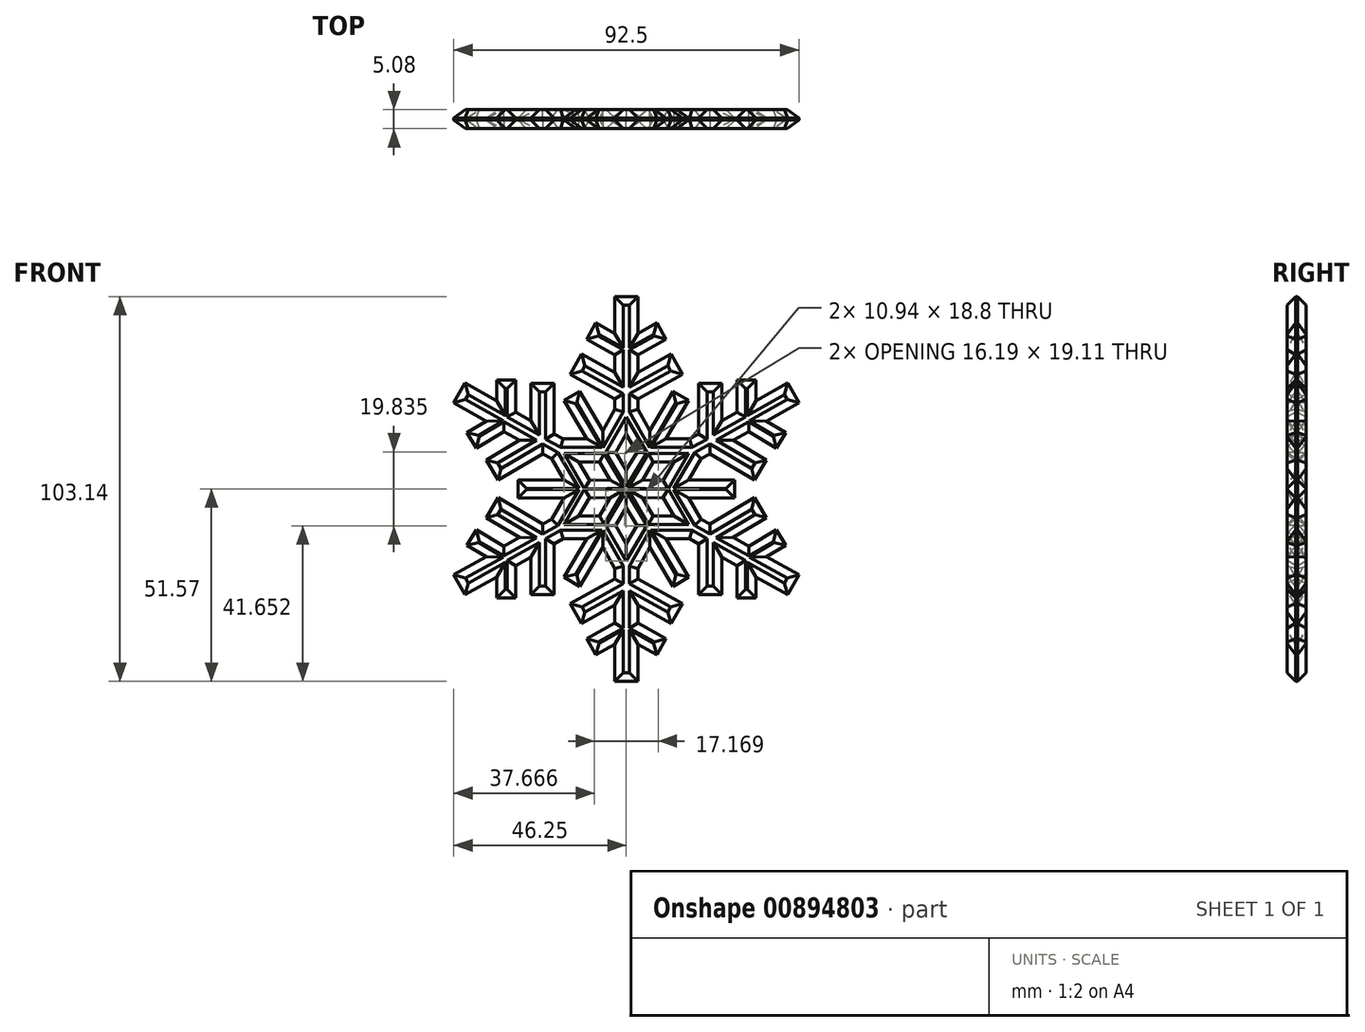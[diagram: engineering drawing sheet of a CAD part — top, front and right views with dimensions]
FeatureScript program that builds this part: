
annotation { "Feature Type Name" : "Feature", "Feature Type Description" : "" }
export const myFeature = defineFeature(function(context is Context, id is Id, definition is map)
    precondition{}
    {
        {
            var Q0;
            Q0=qCreatedBy(makeId("Front.planeOp"),FACE);
            var sketch = newSketch(context, id + "F0", { "sketchPlane" : qUnion([Q0])});
            skLineSegment(sketch, "E0", {"start": v(0, -5) * mm, "end": v(-2.83, -9.77) * mm});
            skLineSegment(sketch, "E1", {"start": v(-2.83, -9.77) * mm, "end": v(0, -14.71) * mm});
            skLineSegment(sketch, "E2", {"start": v(0, -51.57) * mm, "end": v(-3.12, -51.57) * mm});
            skLineSegment(sketch, "E3", {"start": v(-3.12, -51.57) * mm, "end": v(-3.12, -41.68) * mm});
            skLineSegment(sketch, "E4", {"start": v(-3.12, -41.68) * mm, "end": v(-8.18, -44.5) * mm});
            skLineSegment(sketch, "E5", {"start": v(-8.18, -44.5) * mm, "end": v(-10.6, -40.16) * mm});
            skLineSegment(sketch, "E6", {"start": v(-10.6, -40.16) * mm, "end": v(-3.12, -35.98) * mm});
            skLineSegment(sketch, "E7", {"start": v(-3.12, -35.98) * mm, "end": v(-3.12, -31.16) * mm});
            skLineSegment(sketch, "E8", {"start": v(-3.12, -31.16) * mm, "end": v(-12, -36.12) * mm});
            skLineSegment(sketch, "E9", {"start": v(-12, -36.12) * mm, "end": v(-15, -30.75) * mm});
            skLineSegment(sketch, "E10", {"start": v(-15, -30.75) * mm, "end": v(-3.12, -24.11) * mm});
            skLineSegment(sketch, "E11", {"start": v(-3.12, -24.11) * mm, "end": v(-3.12, -21.32) * mm});
            skLineSegment(sketch, "E12", {"start": v(-3.12, -21.32) * mm, "end": v(-6.29, -15.65) * mm});
            skLineSegment(sketch, "E13", {"start": v(-6.29, -15.65) * mm, "end": v(-12.51, -26.16) * mm});
            skLineSegment(sketch, "E14", {"start": v(-12.51, -26.16) * mm, "end": v(-16.68, -23.7) * mm});
            skLineSegment(sketch, "E15", {"start": v(-16.68, -23.7) * mm, "end": v(-10.57, -13.4) * mm});
            skLineSegment(sketch, "E16", {"start": v(-10.57, -13.4) * mm, "end": v(-17, -13.4) * mm});
            skLineSegment(sketch, "E17", {"start": v(-17, -13.4) * mm, "end": v(-19.37, -14.71) * mm});
            skLineSegment(sketch, "E18", {"start": v(-19.37, -14.71) * mm, "end": v(-19.37, -28.34) * mm});
            skLineSegment(sketch, "E19", {"start": v(-19.37, -28.34) * mm, "end": v(-25.64, -28.34) * mm});
            skLineSegment(sketch, "E20", {"start": v(-25.64, -28.34) * mm, "end": v(-25.64, -18.32) * mm});
            skLineSegment(sketch, "E21", {"start": v(-25.64, -18.32) * mm, "end": v(-29.69, -20.58) * mm});
            skLineSegment(sketch, "E22", {"start": v(-29.69, -20.58) * mm, "end": v(-29.69, -29.2) * mm});
            skLineSegment(sketch, "E23", {"start": v(-29.69, -29.2) * mm, "end": v(-34.73, -29.2) * mm});
            skLineSegment(sketch, "E24", {"start": v(-34.73, -29.2) * mm, "end": v(-34.73, -23.6) * mm});
            skLineSegment(sketch, "E25", {"start": v(-34.73, -23.6) * mm, "end": v(-43.27, -28.37) * mm});
            skLineSegment(sketch, "E26", {"start": v(-43.27, -28.37) * mm, "end": v(-46.25, -23.04) * mm});
            skLineSegment(sketch, "E27", {"start": v(-46.25, -23.04) * mm, "end": v(-37.55, -18.19) * mm});
            skLineSegment(sketch, "E28", {"start": v(-37.55, -18.19) * mm, "end": v(-42.7, -15.14) * mm});
            skLineSegment(sketch, "E29", {"start": v(-42.7, -15.14) * mm, "end": v(-40.22, -10.95) * mm});
            skLineSegment(sketch, "E30", {"start": v(-40.22, -10.95) * mm, "end": v(-32.83, -15.33) * mm});
            skLineSegment(sketch, "E31", {"start": v(-32.83, -15.33) * mm, "end": v(-28.66, -13) * mm});
            skLineSegment(sketch, "E32", {"start": v(-28.66, -13) * mm, "end": v(-37.57, -7.73) * mm});
            skLineSegment(sketch, "E33", {"start": v(-37.57, -7.73) * mm, "end": v(-34.38, -2.34) * mm});
            skLineSegment(sketch, "E34", {"start": v(-34.38, -2.34) * mm, "end": v(-22.4, -9.44) * mm});
            skLineSegment(sketch, "E35", {"start": v(-22.4, -9.44) * mm, "end": v(-20.03, -8.12) * mm});
            skLineSegment(sketch, "E36", {"start": v(-20.03, -8.12) * mm, "end": v(-16.64, -2.4) * mm});
            skLineSegment(sketch, "E37", {"start": v(-16.64, -2.4) * mm, "end": v(-29.06, -2.4) * mm});
            skLineSegment(sketch, "E38", {"start": v(-29.06, -2.4) * mm, "end": v(-29.06, 0) * mm});
            skLineSegment(sketch, "E39", {"start": v(0, 0) * mm, "end": v(0, -1.87) * mm});
            skLineSegment(sketch, "E40", {"start": v(0, 0) * mm, "end": v(2.1, 0) * mm});
            skLineSegment(sketch, "E41", {"start": v(0, 0) * mm, "end": v(-2.42, 0) * mm});
            skLineSegment(sketch, "E42", {"start": v(0, 0) * mm, "end": v(0, 1.78) * mm});
            skLineSegment(sketch, "E43.MirrorCS", {"start": v(0, -5) * mm, "end": v(2.83, -9.77) * mm});
            skLineSegment(sketch, "E44.MirrorCS", {"start": v(2.83, -9.77) * mm, "end": v(0, -14.71) * mm});
            skLineSegment(sketch, "E45", {"start": v(-4.39, -2.4) * mm, "end": v(-7.18, -7.27) * mm});
            skLineSegment(sketch, "E46", {"start": v(-7.18, -7.27) * mm, "end": v(-12.74, -7.27) * mm});
            skLineSegment(sketch, "E47", {"start": v(-12.74, -7.27) * mm, "end": v(-9.89, -2.29) * mm});
            skLineSegment(sketch, "E48", {"start": v(-9.89, -2.29) * mm, "end": v(-4.39, -2.4) * mm});
            skLineSegment(sketch, "E49.MirrorCS", {"start": v(4.39, -2.4) * mm, "end": v(7.18, -7.27) * mm});
            skLineSegment(sketch, "E50.MirrorCS", {"start": v(9.89, -2.29) * mm, "end": v(4.39, -2.4) * mm});
            skLineSegment(sketch, "E51.MirrorCS", {"start": v(7.18, -7.27) * mm, "end": v(12.74, -7.27) * mm});
            skLineSegment(sketch, "E52.MirrorCS", {"start": v(12.74, -7.27) * mm, "end": v(9.89, -2.29) * mm});
            skLineSegment(sketch, "E53.MirrorCS", {"start": v(0, -51.57) * mm, "end": v(3.12, -51.57) * mm});
            skLineSegment(sketch, "E54.MirrorCS", {"start": v(3.12, -51.57) * mm, "end": v(3.12, -41.68) * mm});
            skLineSegment(sketch, "E55.MirrorCS", {"start": v(3.12, -41.68) * mm, "end": v(8.18, -44.5) * mm});
            skLineSegment(sketch, "E56.MirrorCS", {"start": v(8.18, -44.5) * mm, "end": v(10.6, -40.16) * mm});
            skLineSegment(sketch, "E57.MirrorCS", {"start": v(10.6, -40.16) * mm, "end": v(3.12, -35.98) * mm});
            skLineSegment(sketch, "E58.MirrorCS", {"start": v(3.12, -35.98) * mm, "end": v(3.12, -31.16) * mm});
            skLineSegment(sketch, "E59.MirrorCS", {"start": v(3.12, -31.16) * mm, "end": v(12, -36.12) * mm});
            skLineSegment(sketch, "E60.MirrorCS", {"start": v(12, -36.12) * mm, "end": v(15, -30.75) * mm});
            skLineSegment(sketch, "E61.MirrorCS", {"start": v(15, -30.75) * mm, "end": v(3.12, -24.11) * mm});
            skLineSegment(sketch, "E62.MirrorCS", {"start": v(3.12, -24.11) * mm, "end": v(3.12, -21.32) * mm});
            skLineSegment(sketch, "E63.MirrorCS", {"start": v(3.12, -21.32) * mm, "end": v(6.29, -15.65) * mm});
            skLineSegment(sketch, "E64.MirrorCS", {"start": v(6.29, -15.65) * mm, "end": v(12.51, -26.16) * mm});
            skLineSegment(sketch, "E65.MirrorCS", {"start": v(12.51, -26.16) * mm, "end": v(16.68, -23.7) * mm});
            skLineSegment(sketch, "E66.MirrorCS", {"start": v(16.68, -23.7) * mm, "end": v(10.57, -13.4) * mm});
            skLineSegment(sketch, "E67.MirrorCS", {"start": v(10.57, -13.4) * mm, "end": v(17, -13.4) * mm});
            skLineSegment(sketch, "E68.MirrorCS", {"start": v(17, -13.4) * mm, "end": v(19.37, -14.71) * mm});
            skLineSegment(sketch, "E69.MirrorCS", {"start": v(19.37, -14.71) * mm, "end": v(19.37, -28.34) * mm});
            skLineSegment(sketch, "E70.MirrorCS", {"start": v(19.37, -28.34) * mm, "end": v(25.64, -28.34) * mm});
            skLineSegment(sketch, "E71.MirrorCS", {"start": v(25.64, -28.34) * mm, "end": v(25.64, -18.32) * mm});
            skLineSegment(sketch, "E72.MirrorCS", {"start": v(25.64, -18.32) * mm, "end": v(29.69, -20.58) * mm});
            skLineSegment(sketch, "E73.MirrorCS", {"start": v(29.69, -20.58) * mm, "end": v(29.69, -29.2) * mm});
            skLineSegment(sketch, "E74.MirrorCS", {"start": v(29.69, -29.2) * mm, "end": v(34.73, -29.2) * mm});
            skLineSegment(sketch, "E75.MirrorCS", {"start": v(34.73, -29.2) * mm, "end": v(34.73, -23.6) * mm});
            skLineSegment(sketch, "E76.MirrorCS", {"start": v(34.73, -23.6) * mm, "end": v(43.27, -28.37) * mm});
            skLineSegment(sketch, "E77.MirrorCS", {"start": v(43.27, -28.37) * mm, "end": v(46.25, -23.04) * mm});
            skLineSegment(sketch, "E78.MirrorCS", {"start": v(46.25, -23.04) * mm, "end": v(37.55, -18.19) * mm});
            skLineSegment(sketch, "E79.MirrorCS", {"start": v(37.55, -18.19) * mm, "end": v(42.7, -15.14) * mm});
            skLineSegment(sketch, "E80.MirrorCS", {"start": v(42.7, -15.14) * mm, "end": v(40.22, -10.95) * mm});
            skLineSegment(sketch, "E81.MirrorCS", {"start": v(40.22, -10.95) * mm, "end": v(32.83, -15.33) * mm});
            skLineSegment(sketch, "E82.MirrorCS", {"start": v(32.83, -15.33) * mm, "end": v(28.66, -13) * mm});
            skLineSegment(sketch, "E83.MirrorCS", {"start": v(28.66, -13) * mm, "end": v(37.57, -7.73) * mm});
            skLineSegment(sketch, "E84.MirrorCS", {"start": v(37.57, -7.73) * mm, "end": v(34.38, -2.34) * mm});
            skLineSegment(sketch, "E85.MirrorCS", {"start": v(34.38, -2.34) * mm, "end": v(22.4, -9.44) * mm});
            skLineSegment(sketch, "E86.MirrorCS", {"start": v(22.4, -9.44) * mm, "end": v(20.03, -8.12) * mm});
            skLineSegment(sketch, "E87.MirrorCS", {"start": v(20.03, -8.12) * mm, "end": v(16.64, -2.4) * mm});
            skLineSegment(sketch, "E88.MirrorCS", {"start": v(16.64, -2.4) * mm, "end": v(29.06, -2.4) * mm});
            skLineSegment(sketch, "E89.MirrorCS", {"start": v(29.06, -2.4) * mm, "end": v(29.06, 0) * mm});
            skLineSegment(sketch, "E90.MirrorCS", {"start": v(9.89, 2.29) * mm, "end": v(4.39, 2.4) * mm});
            skLineSegment(sketch, "E91.MirrorCS", {"start": v(4.39, 2.4) * mm, "end": v(7.18, 7.27) * mm});
            skLineSegment(sketch, "E92.MirrorCS", {"start": v(12.74, 7.27) * mm, "end": v(9.89, 2.29) * mm});
            skLineSegment(sketch, "E93.MirrorCS", {"start": v(7.18, 7.27) * mm, "end": v(12.74, 7.27) * mm});
            skLineSegment(sketch, "E94.MirrorCS", {"start": v(29.06, 2.4) * mm, "end": v(29.06, 0) * mm});
            skLineSegment(sketch, "E95.MirrorCS", {"start": v(16.64, 2.4) * mm, "end": v(29.06, 2.4) * mm});
            skLineSegment(sketch, "E96.MirrorCS", {"start": v(20.03, 8.12) * mm, "end": v(16.64, 2.4) * mm});
            skLineSegment(sketch, "E97.MirrorCS", {"start": v(22.4, 9.44) * mm, "end": v(20.03, 8.12) * mm});
            skLineSegment(sketch, "E98.MirrorCS", {"start": v(34.38, 2.34) * mm, "end": v(22.4, 9.44) * mm});
            skLineSegment(sketch, "E99.MirrorCS", {"start": v(37.57, 7.73) * mm, "end": v(34.38, 2.34) * mm});
            skLineSegment(sketch, "E100.MirrorCS", {"start": v(28.66, 13) * mm, "end": v(37.57, 7.73) * mm});
            skLineSegment(sketch, "E101.MirrorCS", {"start": v(32.83, 15.33) * mm, "end": v(28.66, 13) * mm});
            skLineSegment(sketch, "E102.MirrorCS", {"start": v(40.22, 10.95) * mm, "end": v(32.83, 15.33) * mm});
            skLineSegment(sketch, "E103.MirrorCS", {"start": v(42.7, 15.14) * mm, "end": v(40.22, 10.95) * mm});
            skLineSegment(sketch, "E104.MirrorCS", {"start": v(37.55, 18.19) * mm, "end": v(42.7, 15.14) * mm});
            skLineSegment(sketch, "E105.MirrorCS", {"start": v(46.25, 23.04) * mm, "end": v(37.55, 18.19) * mm});
            skLineSegment(sketch, "E106.MirrorCS", {"start": v(29.69, 20.58) * mm, "end": v(29.69, 29.2) * mm});
            skLineSegment(sketch, "E107.MirrorCS", {"start": v(43.27, 28.37) * mm, "end": v(46.25, 23.04) * mm});
            skLineSegment(sketch, "E108.MirrorCS", {"start": v(25.64, 28.34) * mm, "end": v(25.64, 18.32) * mm});
            skLineSegment(sketch, "E109.MirrorCS", {"start": v(34.73, 29.2) * mm, "end": v(34.73, 23.6) * mm});
            skLineSegment(sketch, "E110.MirrorCS", {"start": v(19.37, 28.34) * mm, "end": v(25.64, 28.34) * mm});
            skLineSegment(sketch, "E111.MirrorCS", {"start": v(29.69, 29.2) * mm, "end": v(34.73, 29.2) * mm});
            skLineSegment(sketch, "E112.MirrorCS", {"start": v(34.73, 23.6) * mm, "end": v(43.27, 28.37) * mm});
            skLineSegment(sketch, "E113.MirrorCS", {"start": v(19.37, 14.71) * mm, "end": v(19.37, 28.34) * mm});
            skLineSegment(sketch, "E114.MirrorCS", {"start": v(-3.12, 24.11) * mm, "end": v(-3.12, 21.32) * mm});
            skLineSegment(sketch, "E115.MirrorCS", {"start": v(-25.64, 18.32) * mm, "end": v(-29.69, 20.58) * mm});
            skLineSegment(sketch, "E116.MirrorCS", {"start": v(-17, 13.4) * mm, "end": v(-19.37, 14.71) * mm});
            skLineSegment(sketch, "E117.MirrorCS", {"start": v(12.51, 26.16) * mm, "end": v(16.68, 23.7) * mm});
            skLineSegment(sketch, "E118.MirrorCS", {"start": v(3.12, 24.11) * mm, "end": v(3.12, 21.32) * mm});
            skLineSegment(sketch, "E119.MirrorCS", {"start": v(12, 36.12) * mm, "end": v(15, 30.75) * mm});
            skLineSegment(sketch, "E120.MirrorCS", {"start": v(3.12, 21.32) * mm, "end": v(6.29, 15.65) * mm});
            skLineSegment(sketch, "E121.MirrorCS", {"start": v(-10.57, 13.4) * mm, "end": v(-17, 13.4) * mm});
            skLineSegment(sketch, "E122.MirrorCS", {"start": v(-28.66, 13) * mm, "end": v(-37.57, 7.73) * mm});
            skLineSegment(sketch, "E123.MirrorCS", {"start": v(-6.29, 15.65) * mm, "end": v(-12.51, 26.16) * mm});
            skLineSegment(sketch, "E124.MirrorCS", {"start": v(3.12, 41.68) * mm, "end": v(8.18, 44.5) * mm});
            skLineSegment(sketch, "E125.MirrorCS", {"start": v(-34.73, 23.6) * mm, "end": v(-43.27, 28.37) * mm});
            skLineSegment(sketch, "E126.MirrorCS", {"start": v(-3.12, 41.68) * mm, "end": v(-8.18, 44.5) * mm});
            skLineSegment(sketch, "E127.MirrorCS", {"start": v(-2.83, 9.77) * mm, "end": v(0, 14.71) * mm});
            skLineSegment(sketch, "E128.MirrorCS", {"start": v(-10.6, 40.16) * mm, "end": v(-3.12, 35.98) * mm});
            skLineSegment(sketch, "E129.MirrorCS", {"start": v(2.83, 9.77) * mm, "end": v(0, 14.71) * mm});
            skLineSegment(sketch, "E130.MirrorCS", {"start": v(10.57, 13.4) * mm, "end": v(17, 13.4) * mm});
            skLineSegment(sketch, "E131.MirrorCS", {"start": v(-3.12, 31.16) * mm, "end": v(-12, 36.12) * mm});
            skLineSegment(sketch, "E132.MirrorCS", {"start": v(-3.12, 51.57) * mm, "end": v(-3.12, 41.68) * mm});
            skLineSegment(sketch, "E133.MirrorCS", {"start": v(-3.12, 35.98) * mm, "end": v(-3.12, 31.16) * mm});
            skLineSegment(sketch, "E134.MirrorCS", {"start": v(-29.69, 20.58) * mm, "end": v(-29.69, 29.2) * mm});
            skLineSegment(sketch, "E135.MirrorCS", {"start": v(-3.12, 21.32) * mm, "end": v(-6.29, 15.65) * mm});
            skLineSegment(sketch, "E136.MirrorCS", {"start": v(-43.27, 28.37) * mm, "end": v(-46.25, 23.04) * mm});
            skLineSegment(sketch, "E137.MirrorCS", {"start": v(-40.22, 10.95) * mm, "end": v(-32.83, 15.33) * mm});
            skLineSegment(sketch, "E138.MirrorCS", {"start": v(-19.37, 14.71) * mm, "end": v(-19.37, 28.34) * mm});
            skLineSegment(sketch, "E139.MirrorCS", {"start": v(-12, 36.12) * mm, "end": v(-15, 30.75) * mm});
            skLineSegment(sketch, "E140.MirrorCS", {"start": v(-42.7, 15.14) * mm, "end": v(-40.22, 10.95) * mm});
            skLineSegment(sketch, "E141.MirrorCS", {"start": v(-25.64, 28.34) * mm, "end": v(-25.64, 18.32) * mm});
            skLineSegment(sketch, "E142.MirrorCS", {"start": v(8.18, 44.5) * mm, "end": v(10.6, 40.16) * mm});
            skLineSegment(sketch, "E143.MirrorCS", {"start": v(-46.25, 23.04) * mm, "end": v(-37.55, 18.19) * mm});
            skLineSegment(sketch, "E144.MirrorCS", {"start": v(-32.83, 15.33) * mm, "end": v(-28.66, 13) * mm});
            skLineSegment(sketch, "E145.MirrorCS", {"start": v(3.12, 51.57) * mm, "end": v(3.12, 41.68) * mm});
            skLineSegment(sketch, "E146.MirrorCS", {"start": v(-12.51, 26.16) * mm, "end": v(-16.68, 23.7) * mm});
            skLineSegment(sketch, "E147.MirrorCS", {"start": v(-8.18, 44.5) * mm, "end": v(-10.6, 40.16) * mm});
            skLineSegment(sketch, "E148.MirrorCS", {"start": v(10.6, 40.16) * mm, "end": v(3.12, 35.98) * mm});
            skLineSegment(sketch, "E149.MirrorCS", {"start": v(3.12, 35.98) * mm, "end": v(3.12, 31.16) * mm});
            skLineSegment(sketch, "E150.MirrorCS", {"start": v(-16.68, 23.7) * mm, "end": v(-10.57, 13.4) * mm});
            skLineSegment(sketch, "E151.MirrorCS", {"start": v(-29.69, 29.2) * mm, "end": v(-34.73, 29.2) * mm});
            skLineSegment(sketch, "E152.MirrorCS", {"start": v(15, 30.75) * mm, "end": v(3.12, 24.11) * mm});
            skLineSegment(sketch, "E153.MirrorCS", {"start": v(-34.73, 29.2) * mm, "end": v(-34.73, 23.6) * mm});
            skLineSegment(sketch, "E154.MirrorCS", {"start": v(16.68, 23.7) * mm, "end": v(10.57, 13.4) * mm});
            skLineSegment(sketch, "E155.MirrorCS", {"start": v(-15, 30.75) * mm, "end": v(-3.12, 24.11) * mm});
            skLineSegment(sketch, "E156.MirrorCS", {"start": v(6.29, 15.65) * mm, "end": v(12.51, 26.16) * mm});
            skLineSegment(sketch, "E157.MirrorCS", {"start": v(-37.55, 18.19) * mm, "end": v(-42.7, 15.14) * mm});
            skLineSegment(sketch, "E158.MirrorCS", {"start": v(3.12, 31.16) * mm, "end": v(12, 36.12) * mm});
            skLineSegment(sketch, "E159.MirrorCS", {"start": v(-19.37, 28.34) * mm, "end": v(-25.64, 28.34) * mm});
            skLineSegment(sketch, "E160.MirrorCS", {"start": v(0, 51.57) * mm, "end": v(-3.12, 51.57) * mm});
            skLineSegment(sketch, "E161.MirrorCS", {"start": v(0, 51.57) * mm, "end": v(3.12, 51.57) * mm});
            skLineSegment(sketch, "E162.MirrorCS", {"start": v(0, 0) * mm, "end": v(0, 1.87) * mm});
            skLineSegment(sketch, "E163.MirrorCS", {"start": v(-22.4, 9.44) * mm, "end": v(-20.03, 8.12) * mm});
            skLineSegment(sketch, "E164.MirrorCS", {"start": v(0, 5) * mm, "end": v(2.83, 9.77) * mm});
            skLineSegment(sketch, "E165.MirrorCS", {"start": v(-29.06, 2.4) * mm, "end": v(-29.06, 0) * mm});
            skLineSegment(sketch, "E166.MirrorCS", {"start": v(0, 5) * mm, "end": v(-2.83, 9.77) * mm});
            skLineSegment(sketch, "E167.MirrorCS", {"start": v(-9.89, 2.29) * mm, "end": v(-4.39, 2.4) * mm});
            skLineSegment(sketch, "E168.MirrorCS", {"start": v(-7.18, 7.27) * mm, "end": v(-12.74, 7.27) * mm});
            skLineSegment(sketch, "E169.MirrorCS", {"start": v(-20.03, 8.12) * mm, "end": v(-16.64, 2.4) * mm});
            skLineSegment(sketch, "E170.MirrorCS", {"start": v(-37.57, 7.73) * mm, "end": v(-34.38, 2.34) * mm});
            skLineSegment(sketch, "E171.MirrorCS", {"start": v(-12.74, 7.27) * mm, "end": v(-9.89, 2.29) * mm});
            skLineSegment(sketch, "E172.MirrorCS", {"start": v(-16.64, 2.4) * mm, "end": v(-29.06, 2.4) * mm});
            skLineSegment(sketch, "E173.MirrorCS", {"start": v(-4.39, 2.4) * mm, "end": v(-7.18, 7.27) * mm});
            skLineSegment(sketch, "E174.MirrorCS", {"start": v(-34.38, 2.34) * mm, "end": v(-22.4, 9.44) * mm});
            skLineSegment(sketch, "E175", {"start": v(17, 13.4) * mm, "end": v(19.37, 14.71) * mm});
            skLineSegment(sketch, "E176", {"start": v(25.64, 18.32) * mm, "end": v(29.69, 20.58) * mm});
            skSolve(sketch);
        }
        {
            var Q0;
            Q0=makeQuery(id+"F0.imprint","IMPRINT",FACE,{"disambiguationData":[TD([[makeQuery(id+"F0.imprint","IMPRINT",EDGE,{"derivedFrom":sQuery(id+"F0.wireOp",EDGE,"E0")}),-1.0]])]});
            extrude(context, id + "F1", {"entities" : qUnion([Q0]), "depth" : 2.54 * mm, "offsetDistance" : 25.4 * mm});
        }
        {
            var Q0;
            Q0=makeQuery(id+"F1.opExtrude","CAP_FACE",FACE,{"disambiguationData":[OSD([sQuery(id+"F0.wireOp",EDGE,"E0"),sQuery(id+"F0.wireOp",EDGE,"E1"),sQuery(id+"F0.wireOp",EDGE,"E2"),sQuery(id+"F0.wireOp",EDGE,"E3"),sQuery(id+"F0.wireOp",EDGE,"E4"),sQuery(id+"F0.wireOp",EDGE,"E5"),sQuery(id+"F0.wireOp",EDGE,"E6"),sQuery(id+"F0.wireOp",EDGE,"E7"),sQuery(id+"F0.wireOp",EDGE,"E8"),sQuery(id+"F0.wireOp",EDGE,"E9"),sQuery(id+"F0.wireOp",EDGE,"E10"),sQuery(id+"F0.wireOp",EDGE,"E11"),sQuery(id+"F0.wireOp",EDGE,"E12"),sQuery(id+"F0.wireOp",EDGE,"E13"),sQuery(id+"F0.wireOp",EDGE,"E14"),sQuery(id+"F0.wireOp",EDGE,"E15"),sQuery(id+"F0.wireOp",EDGE,"E16"),sQuery(id+"F0.wireOp",EDGE,"E17"),sQuery(id+"F0.wireOp",EDGE,"E18"),sQuery(id+"F0.wireOp",EDGE,"E19"),sQuery(id+"F0.wireOp",EDGE,"E20"),sQuery(id+"F0.wireOp",EDGE,"E21"),sQuery(id+"F0.wireOp",EDGE,"E22"),sQuery(id+"F0.wireOp",EDGE,"E23"),sQuery(id+"F0.wireOp",EDGE,"E24"),sQuery(id+"F0.wireOp",EDGE,"E25"),sQuery(id+"F0.wireOp",EDGE,"E26"),sQuery(id+"F0.wireOp",EDGE,"E27"),sQuery(id+"F0.wireOp",EDGE,"E28"),sQuery(id+"F0.wireOp",EDGE,"E29"),sQuery(id+"F0.wireOp",EDGE,"E30"),sQuery(id+"F0.wireOp",EDGE,"E31"),sQuery(id+"F0.wireOp",EDGE,"E32"),sQuery(id+"F0.wireOp",EDGE,"E33"),sQuery(id+"F0.wireOp",EDGE,"E34"),sQuery(id+"F0.wireOp",EDGE,"E35"),sQuery(id+"F0.wireOp",EDGE,"E36"),sQuery(id+"F0.wireOp",EDGE,"E37"),sQuery(id+"F0.wireOp",EDGE,"E38"),sQuery(id+"F0.wireOp",EDGE,"E43.MirrorCS"),sQuery(id+"F0.wireOp",EDGE,"E44.MirrorCS"),sQuery(id+"F0.wireOp",EDGE,"E45"),sQuery(id+"F0.wireOp",EDGE,"E46"),sQuery(id+"F0.wireOp",EDGE,"E47"),sQuery(id+"F0.wireOp",EDGE,"E48"),sQuery(id+"F0.wireOp",EDGE,"E49.MirrorCS"),sQuery(id+"F0.wireOp",EDGE,"E50.MirrorCS"),sQuery(id+"F0.wireOp",EDGE,"E51.MirrorCS"),sQuery(id+"F0.wireOp",EDGE,"E52.MirrorCS"),sQuery(id+"F0.wireOp",EDGE,"E53.MirrorCS"),sQuery(id+"F0.wireOp",EDGE,"E54.MirrorCS"),sQuery(id+"F0.wireOp",EDGE,"E55.MirrorCS"),sQuery(id+"F0.wireOp",EDGE,"E56.MirrorCS"),sQuery(id+"F0.wireOp",EDGE,"E57.MirrorCS"),sQuery(id+"F0.wireOp",EDGE,"E58.MirrorCS"),sQuery(id+"F0.wireOp",EDGE,"E59.MirrorCS"),sQuery(id+"F0.wireOp",EDGE,"E60.MirrorCS"),sQuery(id+"F0.wireOp",EDGE,"E61.MirrorCS"),sQuery(id+"F0.wireOp",EDGE,"E62.MirrorCS"),sQuery(id+"F0.wireOp",EDGE,"E63.MirrorCS"),sQuery(id+"F0.wireOp",EDGE,"E64.MirrorCS"),sQuery(id+"F0.wireOp",EDGE,"E65.MirrorCS"),sQuery(id+"F0.wireOp",EDGE,"E66.MirrorCS"),sQuery(id+"F0.wireOp",EDGE,"E67.MirrorCS"),sQuery(id+"F0.wireOp",EDGE,"E68.MirrorCS"),sQuery(id+"F0.wireOp",EDGE,"E69.MirrorCS"),sQuery(id+"F0.wireOp",EDGE,"E70.MirrorCS"),sQuery(id+"F0.wireOp",EDGE,"E71.MirrorCS"),sQuery(id+"F0.wireOp",EDGE,"E72.MirrorCS"),sQuery(id+"F0.wireOp",EDGE,"E73.MirrorCS"),sQuery(id+"F0.wireOp",EDGE,"E74.MirrorCS"),sQuery(id+"F0.wireOp",EDGE,"E75.MirrorCS"),sQuery(id+"F0.wireOp",EDGE,"E76.MirrorCS"),sQuery(id+"F0.wireOp",EDGE,"E77.MirrorCS"),sQuery(id+"F0.wireOp",EDGE,"E78.MirrorCS"),sQuery(id+"F0.wireOp",EDGE,"E79.MirrorCS"),sQuery(id+"F0.wireOp",EDGE,"E80.MirrorCS"),sQuery(id+"F0.wireOp",EDGE,"E81.MirrorCS"),sQuery(id+"F0.wireOp",EDGE,"E82.MirrorCS"),sQuery(id+"F0.wireOp",EDGE,"E83.MirrorCS"),sQuery(id+"F0.wireOp",EDGE,"E84.MirrorCS"),sQuery(id+"F0.wireOp",EDGE,"E85.MirrorCS"),sQuery(id+"F0.wireOp",EDGE,"E86.MirrorCS"),sQuery(id+"F0.wireOp",EDGE,"E87.MirrorCS"),sQuery(id+"F0.wireOp",EDGE,"E88.MirrorCS"),sQuery(id+"F0.wireOp",EDGE,"E89.MirrorCS"),sQuery(id+"F0.wireOp",EDGE,"E94.MirrorCS"),sQuery(id+"F0.wireOp",EDGE,"E95.MirrorCS"),sQuery(id+"F0.wireOp",EDGE,"E96.MirrorCS"),sQuery(id+"F0.wireOp",EDGE,"E97.MirrorCS"),sQuery(id+"F0.wireOp",EDGE,"E98.MirrorCS"),sQuery(id+"F0.wireOp",EDGE,"E99.MirrorCS"),sQuery(id+"F0.wireOp",EDGE,"E100.MirrorCS"),sQuery(id+"F0.wireOp",EDGE,"E101.MirrorCS"),sQuery(id+"F0.wireOp",EDGE,"E102.MirrorCS"),sQuery(id+"F0.wireOp",EDGE,"E103.MirrorCS"),sQuery(id+"F0.wireOp",EDGE,"E104.MirrorCS"),sQuery(id+"F0.wireOp",EDGE,"E105.MirrorCS"),sQuery(id+"F0.wireOp",EDGE,"E106.MirrorCS"),sQuery(id+"F0.wireOp",EDGE,"E107.MirrorCS"),sQuery(id+"F0.wireOp",EDGE,"E108.MirrorCS"),sQuery(id+"F0.wireOp",EDGE,"E109.MirrorCS"),sQuery(id+"F0.wireOp",EDGE,"E110.MirrorCS"),sQuery(id+"F0.wireOp",EDGE,"E111.MirrorCS"),sQuery(id+"F0.wireOp",EDGE,"E112.MirrorCS"),sQuery(id+"F0.wireOp",EDGE,"E113.MirrorCS"),sQuery(id+"F0.wireOp",EDGE,"E149.MirrorCS"),sQuery(id+"F0.wireOp",EDGE,"E140.MirrorCS"),sQuery(id+"F0.wireOp",EDGE,"E161.MirrorCS"),sQuery(id+"F0.wireOp",EDGE,"E144.MirrorCS"),sQuery(id+"F0.wireOp",EDGE,"E163.MirrorCS"),sQuery(id+"F0.wireOp",EDGE,"E115.MirrorCS"),sQuery(id+"F0.wireOp",EDGE,"E160.MirrorCS"),sQuery(id+"F0.wireOp",EDGE,"E164.MirrorCS"),sQuery(id+"F0.wireOp",EDGE,"E117.MirrorCS"),sQuery(id+"F0.wireOp",EDGE,"E118.MirrorCS"),sQuery(id+"F0.wireOp",EDGE,"E165.MirrorCS"),sQuery(id+"F0.wireOp",EDGE,"E146.MirrorCS"),sQuery(id+"F0.wireOp",EDGE,"E114.MirrorCS"),sQuery(id+"F0.wireOp",EDGE,"E133.MirrorCS"),sQuery(id+"F0.wireOp",EDGE,"E166.MirrorCS"),sQuery(id+"F0.wireOp",EDGE,"E116.MirrorCS"),sQuery(id+"F0.wireOp",EDGE,"E167.MirrorCS"),sQuery(id+"F0.wireOp",EDGE,"E120.MirrorCS"),sQuery(id+"F0.wireOp",EDGE,"E137.MirrorCS"),sQuery(id+"F0.wireOp",EDGE,"E119.MirrorCS"),sQuery(id+"F0.wireOp",EDGE,"E168.MirrorCS"),sQuery(id+"F0.wireOp",EDGE,"E142.MirrorCS"),sQuery(id+"F0.wireOp",EDGE,"E169.MirrorCS"),sQuery(id+"F0.wireOp",EDGE,"E151.MirrorCS"),sQuery(id+"F0.wireOp",EDGE,"E127.MirrorCS"),sQuery(id+"F0.wireOp",EDGE,"E136.MirrorCS"),sQuery(id+"F0.wireOp",EDGE,"E121.MirrorCS"),sQuery(id+"F0.wireOp",EDGE,"E126.MirrorCS"),sQuery(id+"F0.wireOp",EDGE,"E170.MirrorCS"),sQuery(id+"F0.wireOp",EDGE,"E90.MirrorCS"),sQuery(id+"F0.wireOp",EDGE,"E145.MirrorCS"),sQuery(id+"F0.wireOp",EDGE,"E128.MirrorCS"),sQuery(id+"F0.wireOp",EDGE,"E153.MirrorCS"),sQuery(id+"F0.wireOp",EDGE,"E152.MirrorCS"),sQuery(id+"F0.wireOp",EDGE,"E148.MirrorCS"),sQuery(id+"F0.wireOp",EDGE,"E155.MirrorCS"),sQuery(id+"F0.wireOp",EDGE,"E171.MirrorCS"),sQuery(id+"F0.wireOp",EDGE,"E172.MirrorCS"),sQuery(id+"F0.wireOp",EDGE,"E154.MirrorCS"),sQuery(id+"F0.wireOp",EDGE,"E173.MirrorCS"),sQuery(id+"F0.wireOp",EDGE,"E159.MirrorCS"),sQuery(id+"F0.wireOp",EDGE,"E123.MirrorCS"),sQuery(id+"F0.wireOp",EDGE,"E157.MirrorCS"),sQuery(id+"F0.wireOp",EDGE,"E132.MirrorCS"),sQuery(id+"F0.wireOp",EDGE,"E147.MirrorCS"),sQuery(id+"F0.wireOp",EDGE,"E174.MirrorCS"),sQuery(id+"F0.wireOp",EDGE,"E156.MirrorCS"),sQuery(id+"F0.wireOp",EDGE,"E141.MirrorCS"),sQuery(id+"F0.wireOp",EDGE,"E92.MirrorCS"),sQuery(id+"F0.wireOp",EDGE,"E131.MirrorCS"),sQuery(id+"F0.wireOp",EDGE,"E122.MirrorCS"),sQuery(id+"F0.wireOp",EDGE,"E135.MirrorCS"),sQuery(id+"F0.wireOp",EDGE,"E125.MirrorCS"),sQuery(id+"F0.wireOp",EDGE,"E91.MirrorCS"),sQuery(id+"F0.wireOp",EDGE,"E150.MirrorCS"),sQuery(id+"F0.wireOp",EDGE,"E124.MirrorCS"),sQuery(id+"F0.wireOp",EDGE,"E158.MirrorCS"),sQuery(id+"F0.wireOp",EDGE,"E134.MirrorCS"),sQuery(id+"F0.wireOp",EDGE,"E93.MirrorCS"),sQuery(id+"F0.wireOp",EDGE,"E139.MirrorCS"),sQuery(id+"F0.wireOp",EDGE,"E138.MirrorCS"),sQuery(id+"F0.wireOp",EDGE,"E143.MirrorCS"),sQuery(id+"F0.wireOp",EDGE,"E130.MirrorCS"),sQuery(id+"F0.wireOp",EDGE,"E129.MirrorCS"),sQuery(id+"F0.wireOp",EDGE,"E175"),sQuery(id+"F0.wireOp",EDGE,"E176")])],"isStart":true});
            extrude(context, id + "F2", {"entities" : qUnion([Q0]), "operationType" : NewBodyOperationType.ADD, "depth" : 2.54 * mm, "offsetDistance" : 25.4 * mm});
        }
        {
            var Q0;
            Q0=makeQuery(id+"F1.opExtrude","CAP_FACE",FACE,{"disambiguationData":[OSD([sQuery(id+"F0.wireOp",EDGE,"E0"),sQuery(id+"F0.wireOp",EDGE,"E1"),sQuery(id+"F0.wireOp",EDGE,"E2"),sQuery(id+"F0.wireOp",EDGE,"E3"),sQuery(id+"F0.wireOp",EDGE,"E4"),sQuery(id+"F0.wireOp",EDGE,"E5"),sQuery(id+"F0.wireOp",EDGE,"E6"),sQuery(id+"F0.wireOp",EDGE,"E7"),sQuery(id+"F0.wireOp",EDGE,"E8"),sQuery(id+"F0.wireOp",EDGE,"E9"),sQuery(id+"F0.wireOp",EDGE,"E10"),sQuery(id+"F0.wireOp",EDGE,"E11"),sQuery(id+"F0.wireOp",EDGE,"E12"),sQuery(id+"F0.wireOp",EDGE,"E13"),sQuery(id+"F0.wireOp",EDGE,"E14"),sQuery(id+"F0.wireOp",EDGE,"E15"),sQuery(id+"F0.wireOp",EDGE,"E16"),sQuery(id+"F0.wireOp",EDGE,"E17"),sQuery(id+"F0.wireOp",EDGE,"E18"),sQuery(id+"F0.wireOp",EDGE,"E19"),sQuery(id+"F0.wireOp",EDGE,"E20"),sQuery(id+"F0.wireOp",EDGE,"E21"),sQuery(id+"F0.wireOp",EDGE,"E22"),sQuery(id+"F0.wireOp",EDGE,"E23"),sQuery(id+"F0.wireOp",EDGE,"E24"),sQuery(id+"F0.wireOp",EDGE,"E25"),sQuery(id+"F0.wireOp",EDGE,"E26"),sQuery(id+"F0.wireOp",EDGE,"E27"),sQuery(id+"F0.wireOp",EDGE,"E28"),sQuery(id+"F0.wireOp",EDGE,"E29"),sQuery(id+"F0.wireOp",EDGE,"E30"),sQuery(id+"F0.wireOp",EDGE,"E31"),sQuery(id+"F0.wireOp",EDGE,"E32"),sQuery(id+"F0.wireOp",EDGE,"E33"),sQuery(id+"F0.wireOp",EDGE,"E34"),sQuery(id+"F0.wireOp",EDGE,"E35"),sQuery(id+"F0.wireOp",EDGE,"E36"),sQuery(id+"F0.wireOp",EDGE,"E37"),sQuery(id+"F0.wireOp",EDGE,"E38"),sQuery(id+"F0.wireOp",EDGE,"E43.MirrorCS"),sQuery(id+"F0.wireOp",EDGE,"E44.MirrorCS"),sQuery(id+"F0.wireOp",EDGE,"E45"),sQuery(id+"F0.wireOp",EDGE,"E46"),sQuery(id+"F0.wireOp",EDGE,"E47"),sQuery(id+"F0.wireOp",EDGE,"E48"),sQuery(id+"F0.wireOp",EDGE,"E49.MirrorCS"),sQuery(id+"F0.wireOp",EDGE,"E50.MirrorCS"),sQuery(id+"F0.wireOp",EDGE,"E51.MirrorCS"),sQuery(id+"F0.wireOp",EDGE,"E52.MirrorCS"),sQuery(id+"F0.wireOp",EDGE,"E53.MirrorCS"),sQuery(id+"F0.wireOp",EDGE,"E54.MirrorCS"),sQuery(id+"F0.wireOp",EDGE,"E55.MirrorCS"),sQuery(id+"F0.wireOp",EDGE,"E56.MirrorCS"),sQuery(id+"F0.wireOp",EDGE,"E57.MirrorCS"),sQuery(id+"F0.wireOp",EDGE,"E58.MirrorCS"),sQuery(id+"F0.wireOp",EDGE,"E59.MirrorCS"),sQuery(id+"F0.wireOp",EDGE,"E60.MirrorCS"),sQuery(id+"F0.wireOp",EDGE,"E61.MirrorCS"),sQuery(id+"F0.wireOp",EDGE,"E62.MirrorCS"),sQuery(id+"F0.wireOp",EDGE,"E63.MirrorCS"),sQuery(id+"F0.wireOp",EDGE,"E64.MirrorCS"),sQuery(id+"F0.wireOp",EDGE,"E65.MirrorCS"),sQuery(id+"F0.wireOp",EDGE,"E66.MirrorCS"),sQuery(id+"F0.wireOp",EDGE,"E67.MirrorCS"),sQuery(id+"F0.wireOp",EDGE,"E68.MirrorCS"),sQuery(id+"F0.wireOp",EDGE,"E69.MirrorCS"),sQuery(id+"F0.wireOp",EDGE,"E70.MirrorCS"),sQuery(id+"F0.wireOp",EDGE,"E71.MirrorCS"),sQuery(id+"F0.wireOp",EDGE,"E72.MirrorCS"),sQuery(id+"F0.wireOp",EDGE,"E73.MirrorCS"),sQuery(id+"F0.wireOp",EDGE,"E74.MirrorCS"),sQuery(id+"F0.wireOp",EDGE,"E75.MirrorCS"),sQuery(id+"F0.wireOp",EDGE,"E76.MirrorCS"),sQuery(id+"F0.wireOp",EDGE,"E77.MirrorCS"),sQuery(id+"F0.wireOp",EDGE,"E78.MirrorCS"),sQuery(id+"F0.wireOp",EDGE,"E79.MirrorCS"),sQuery(id+"F0.wireOp",EDGE,"E80.MirrorCS"),sQuery(id+"F0.wireOp",EDGE,"E81.MirrorCS"),sQuery(id+"F0.wireOp",EDGE,"E82.MirrorCS"),sQuery(id+"F0.wireOp",EDGE,"E83.MirrorCS"),sQuery(id+"F0.wireOp",EDGE,"E84.MirrorCS"),sQuery(id+"F0.wireOp",EDGE,"E85.MirrorCS"),sQuery(id+"F0.wireOp",EDGE,"E86.MirrorCS"),sQuery(id+"F0.wireOp",EDGE,"E87.MirrorCS"),sQuery(id+"F0.wireOp",EDGE,"E88.MirrorCS"),sQuery(id+"F0.wireOp",EDGE,"E89.MirrorCS"),sQuery(id+"F0.wireOp",EDGE,"E94.MirrorCS"),sQuery(id+"F0.wireOp",EDGE,"E95.MirrorCS"),sQuery(id+"F0.wireOp",EDGE,"E96.MirrorCS"),sQuery(id+"F0.wireOp",EDGE,"E97.MirrorCS"),sQuery(id+"F0.wireOp",EDGE,"E98.MirrorCS"),sQuery(id+"F0.wireOp",EDGE,"E99.MirrorCS"),sQuery(id+"F0.wireOp",EDGE,"E100.MirrorCS"),sQuery(id+"F0.wireOp",EDGE,"E101.MirrorCS"),sQuery(id+"F0.wireOp",EDGE,"E102.MirrorCS"),sQuery(id+"F0.wireOp",EDGE,"E103.MirrorCS"),sQuery(id+"F0.wireOp",EDGE,"E104.MirrorCS"),sQuery(id+"F0.wireOp",EDGE,"E105.MirrorCS"),sQuery(id+"F0.wireOp",EDGE,"E106.MirrorCS"),sQuery(id+"F0.wireOp",EDGE,"E107.MirrorCS"),sQuery(id+"F0.wireOp",EDGE,"E108.MirrorCS"),sQuery(id+"F0.wireOp",EDGE,"E109.MirrorCS"),sQuery(id+"F0.wireOp",EDGE,"E110.MirrorCS"),sQuery(id+"F0.wireOp",EDGE,"E111.MirrorCS"),sQuery(id+"F0.wireOp",EDGE,"E112.MirrorCS"),sQuery(id+"F0.wireOp",EDGE,"E113.MirrorCS"),sQuery(id+"F0.wireOp",EDGE,"E149.MirrorCS"),sQuery(id+"F0.wireOp",EDGE,"E140.MirrorCS"),sQuery(id+"F0.wireOp",EDGE,"E161.MirrorCS"),sQuery(id+"F0.wireOp",EDGE,"E144.MirrorCS"),sQuery(id+"F0.wireOp",EDGE,"E163.MirrorCS"),sQuery(id+"F0.wireOp",EDGE,"E115.MirrorCS"),sQuery(id+"F0.wireOp",EDGE,"E160.MirrorCS"),sQuery(id+"F0.wireOp",EDGE,"E164.MirrorCS"),sQuery(id+"F0.wireOp",EDGE,"E117.MirrorCS"),sQuery(id+"F0.wireOp",EDGE,"E118.MirrorCS"),sQuery(id+"F0.wireOp",EDGE,"E165.MirrorCS"),sQuery(id+"F0.wireOp",EDGE,"E146.MirrorCS"),sQuery(id+"F0.wireOp",EDGE,"E114.MirrorCS"),sQuery(id+"F0.wireOp",EDGE,"E133.MirrorCS"),sQuery(id+"F0.wireOp",EDGE,"E166.MirrorCS"),sQuery(id+"F0.wireOp",EDGE,"E116.MirrorCS"),sQuery(id+"F0.wireOp",EDGE,"E167.MirrorCS"),sQuery(id+"F0.wireOp",EDGE,"E120.MirrorCS"),sQuery(id+"F0.wireOp",EDGE,"E137.MirrorCS"),sQuery(id+"F0.wireOp",EDGE,"E119.MirrorCS"),sQuery(id+"F0.wireOp",EDGE,"E168.MirrorCS"),sQuery(id+"F0.wireOp",EDGE,"E142.MirrorCS"),sQuery(id+"F0.wireOp",EDGE,"E169.MirrorCS"),sQuery(id+"F0.wireOp",EDGE,"E151.MirrorCS"),sQuery(id+"F0.wireOp",EDGE,"E127.MirrorCS"),sQuery(id+"F0.wireOp",EDGE,"E136.MirrorCS"),sQuery(id+"F0.wireOp",EDGE,"E121.MirrorCS"),sQuery(id+"F0.wireOp",EDGE,"E126.MirrorCS"),sQuery(id+"F0.wireOp",EDGE,"E170.MirrorCS"),sQuery(id+"F0.wireOp",EDGE,"E90.MirrorCS"),sQuery(id+"F0.wireOp",EDGE,"E145.MirrorCS"),sQuery(id+"F0.wireOp",EDGE,"E128.MirrorCS"),sQuery(id+"F0.wireOp",EDGE,"E153.MirrorCS"),sQuery(id+"F0.wireOp",EDGE,"E152.MirrorCS"),sQuery(id+"F0.wireOp",EDGE,"E148.MirrorCS"),sQuery(id+"F0.wireOp",EDGE,"E155.MirrorCS"),sQuery(id+"F0.wireOp",EDGE,"E171.MirrorCS"),sQuery(id+"F0.wireOp",EDGE,"E172.MirrorCS"),sQuery(id+"F0.wireOp",EDGE,"E154.MirrorCS"),sQuery(id+"F0.wireOp",EDGE,"E173.MirrorCS"),sQuery(id+"F0.wireOp",EDGE,"E159.MirrorCS"),sQuery(id+"F0.wireOp",EDGE,"E123.MirrorCS"),sQuery(id+"F0.wireOp",EDGE,"E157.MirrorCS"),sQuery(id+"F0.wireOp",EDGE,"E132.MirrorCS"),sQuery(id+"F0.wireOp",EDGE,"E147.MirrorCS"),sQuery(id+"F0.wireOp",EDGE,"E174.MirrorCS"),sQuery(id+"F0.wireOp",EDGE,"E156.MirrorCS"),sQuery(id+"F0.wireOp",EDGE,"E141.MirrorCS"),sQuery(id+"F0.wireOp",EDGE,"E92.MirrorCS"),sQuery(id+"F0.wireOp",EDGE,"E131.MirrorCS"),sQuery(id+"F0.wireOp",EDGE,"E122.MirrorCS"),sQuery(id+"F0.wireOp",EDGE,"E135.MirrorCS"),sQuery(id+"F0.wireOp",EDGE,"E125.MirrorCS"),sQuery(id+"F0.wireOp",EDGE,"E91.MirrorCS"),sQuery(id+"F0.wireOp",EDGE,"E150.MirrorCS"),sQuery(id+"F0.wireOp",EDGE,"E124.MirrorCS"),sQuery(id+"F0.wireOp",EDGE,"E158.MirrorCS"),sQuery(id+"F0.wireOp",EDGE,"E134.MirrorCS"),sQuery(id+"F0.wireOp",EDGE,"E93.MirrorCS"),sQuery(id+"F0.wireOp",EDGE,"E139.MirrorCS"),sQuery(id+"F0.wireOp",EDGE,"E138.MirrorCS"),sQuery(id+"F0.wireOp",EDGE,"E143.MirrorCS"),sQuery(id+"F0.wireOp",EDGE,"E130.MirrorCS"),sQuery(id+"F0.wireOp",EDGE,"E129.MirrorCS"),sQuery(id+"F0.wireOp",EDGE,"E175"),sQuery(id+"F0.wireOp",EDGE,"E176")])],"isStart":false});
            var Q1;
            Q1=makeQuery(id+"F2.opExtrude","CAP_FACE",FACE,{"disambiguationData":[OSD([sQuery(id+"F0.wireOp",EDGE,"E0"),sQuery(id+"F0.wireOp",EDGE,"E1"),sQuery(id+"F0.wireOp",EDGE,"E2"),sQuery(id+"F0.wireOp",EDGE,"E3"),sQuery(id+"F0.wireOp",EDGE,"E4"),sQuery(id+"F0.wireOp",EDGE,"E5"),sQuery(id+"F0.wireOp",EDGE,"E6"),sQuery(id+"F0.wireOp",EDGE,"E7"),sQuery(id+"F0.wireOp",EDGE,"E8"),sQuery(id+"F0.wireOp",EDGE,"E9"),sQuery(id+"F0.wireOp",EDGE,"E10"),sQuery(id+"F0.wireOp",EDGE,"E11"),sQuery(id+"F0.wireOp",EDGE,"E12"),sQuery(id+"F0.wireOp",EDGE,"E13"),sQuery(id+"F0.wireOp",EDGE,"E14"),sQuery(id+"F0.wireOp",EDGE,"E15"),sQuery(id+"F0.wireOp",EDGE,"E16"),sQuery(id+"F0.wireOp",EDGE,"E17"),sQuery(id+"F0.wireOp",EDGE,"E18"),sQuery(id+"F0.wireOp",EDGE,"E19"),sQuery(id+"F0.wireOp",EDGE,"E20"),sQuery(id+"F0.wireOp",EDGE,"E21"),sQuery(id+"F0.wireOp",EDGE,"E22"),sQuery(id+"F0.wireOp",EDGE,"E23"),sQuery(id+"F0.wireOp",EDGE,"E24"),sQuery(id+"F0.wireOp",EDGE,"E25"),sQuery(id+"F0.wireOp",EDGE,"E26"),sQuery(id+"F0.wireOp",EDGE,"E27"),sQuery(id+"F0.wireOp",EDGE,"E28"),sQuery(id+"F0.wireOp",EDGE,"E29"),sQuery(id+"F0.wireOp",EDGE,"E30"),sQuery(id+"F0.wireOp",EDGE,"E31"),sQuery(id+"F0.wireOp",EDGE,"E32"),sQuery(id+"F0.wireOp",EDGE,"E33"),sQuery(id+"F0.wireOp",EDGE,"E34"),sQuery(id+"F0.wireOp",EDGE,"E35"),sQuery(id+"F0.wireOp",EDGE,"E36"),sQuery(id+"F0.wireOp",EDGE,"E37"),sQuery(id+"F0.wireOp",EDGE,"E38"),sQuery(id+"F0.wireOp",EDGE,"E43.MirrorCS"),sQuery(id+"F0.wireOp",EDGE,"E44.MirrorCS"),sQuery(id+"F0.wireOp",EDGE,"E45"),sQuery(id+"F0.wireOp",EDGE,"E46"),sQuery(id+"F0.wireOp",EDGE,"E47"),sQuery(id+"F0.wireOp",EDGE,"E48"),sQuery(id+"F0.wireOp",EDGE,"E49.MirrorCS"),sQuery(id+"F0.wireOp",EDGE,"E50.MirrorCS"),sQuery(id+"F0.wireOp",EDGE,"E51.MirrorCS"),sQuery(id+"F0.wireOp",EDGE,"E52.MirrorCS"),sQuery(id+"F0.wireOp",EDGE,"E53.MirrorCS"),sQuery(id+"F0.wireOp",EDGE,"E54.MirrorCS"),sQuery(id+"F0.wireOp",EDGE,"E55.MirrorCS"),sQuery(id+"F0.wireOp",EDGE,"E56.MirrorCS"),sQuery(id+"F0.wireOp",EDGE,"E57.MirrorCS"),sQuery(id+"F0.wireOp",EDGE,"E58.MirrorCS"),sQuery(id+"F0.wireOp",EDGE,"E59.MirrorCS"),sQuery(id+"F0.wireOp",EDGE,"E60.MirrorCS"),sQuery(id+"F0.wireOp",EDGE,"E61.MirrorCS"),sQuery(id+"F0.wireOp",EDGE,"E62.MirrorCS"),sQuery(id+"F0.wireOp",EDGE,"E63.MirrorCS"),sQuery(id+"F0.wireOp",EDGE,"E64.MirrorCS"),sQuery(id+"F0.wireOp",EDGE,"E65.MirrorCS"),sQuery(id+"F0.wireOp",EDGE,"E66.MirrorCS"),sQuery(id+"F0.wireOp",EDGE,"E67.MirrorCS"),sQuery(id+"F0.wireOp",EDGE,"E68.MirrorCS"),sQuery(id+"F0.wireOp",EDGE,"E69.MirrorCS"),sQuery(id+"F0.wireOp",EDGE,"E70.MirrorCS"),sQuery(id+"F0.wireOp",EDGE,"E71.MirrorCS"),sQuery(id+"F0.wireOp",EDGE,"E72.MirrorCS"),sQuery(id+"F0.wireOp",EDGE,"E73.MirrorCS"),sQuery(id+"F0.wireOp",EDGE,"E74.MirrorCS"),sQuery(id+"F0.wireOp",EDGE,"E75.MirrorCS"),sQuery(id+"F0.wireOp",EDGE,"E76.MirrorCS"),sQuery(id+"F0.wireOp",EDGE,"E77.MirrorCS"),sQuery(id+"F0.wireOp",EDGE,"E78.MirrorCS"),sQuery(id+"F0.wireOp",EDGE,"E79.MirrorCS"),sQuery(id+"F0.wireOp",EDGE,"E80.MirrorCS"),sQuery(id+"F0.wireOp",EDGE,"E81.MirrorCS"),sQuery(id+"F0.wireOp",EDGE,"E82.MirrorCS"),sQuery(id+"F0.wireOp",EDGE,"E83.MirrorCS"),sQuery(id+"F0.wireOp",EDGE,"E84.MirrorCS"),sQuery(id+"F0.wireOp",EDGE,"E85.MirrorCS"),sQuery(id+"F0.wireOp",EDGE,"E86.MirrorCS"),sQuery(id+"F0.wireOp",EDGE,"E87.MirrorCS"),sQuery(id+"F0.wireOp",EDGE,"E88.MirrorCS"),sQuery(id+"F0.wireOp",EDGE,"E89.MirrorCS"),sQuery(id+"F0.wireOp",EDGE,"E94.MirrorCS"),sQuery(id+"F0.wireOp",EDGE,"E95.MirrorCS"),sQuery(id+"F0.wireOp",EDGE,"E96.MirrorCS"),sQuery(id+"F0.wireOp",EDGE,"E97.MirrorCS"),sQuery(id+"F0.wireOp",EDGE,"E98.MirrorCS"),sQuery(id+"F0.wireOp",EDGE,"E99.MirrorCS"),sQuery(id+"F0.wireOp",EDGE,"E100.MirrorCS"),sQuery(id+"F0.wireOp",EDGE,"E101.MirrorCS"),sQuery(id+"F0.wireOp",EDGE,"E102.MirrorCS"),sQuery(id+"F0.wireOp",EDGE,"E103.MirrorCS"),sQuery(id+"F0.wireOp",EDGE,"E104.MirrorCS"),sQuery(id+"F0.wireOp",EDGE,"E105.MirrorCS"),sQuery(id+"F0.wireOp",EDGE,"E106.MirrorCS"),sQuery(id+"F0.wireOp",EDGE,"E107.MirrorCS"),sQuery(id+"F0.wireOp",EDGE,"E108.MirrorCS"),sQuery(id+"F0.wireOp",EDGE,"E109.MirrorCS"),sQuery(id+"F0.wireOp",EDGE,"E110.MirrorCS"),sQuery(id+"F0.wireOp",EDGE,"E111.MirrorCS"),sQuery(id+"F0.wireOp",EDGE,"E112.MirrorCS"),sQuery(id+"F0.wireOp",EDGE,"E113.MirrorCS"),sQuery(id+"F0.wireOp",EDGE,"E149.MirrorCS"),sQuery(id+"F0.wireOp",EDGE,"E140.MirrorCS"),sQuery(id+"F0.wireOp",EDGE,"E161.MirrorCS"),sQuery(id+"F0.wireOp",EDGE,"E144.MirrorCS"),sQuery(id+"F0.wireOp",EDGE,"E163.MirrorCS"),sQuery(id+"F0.wireOp",EDGE,"E115.MirrorCS"),sQuery(id+"F0.wireOp",EDGE,"E160.MirrorCS"),sQuery(id+"F0.wireOp",EDGE,"E164.MirrorCS"),sQuery(id+"F0.wireOp",EDGE,"E117.MirrorCS"),sQuery(id+"F0.wireOp",EDGE,"E118.MirrorCS"),sQuery(id+"F0.wireOp",EDGE,"E165.MirrorCS"),sQuery(id+"F0.wireOp",EDGE,"E146.MirrorCS"),sQuery(id+"F0.wireOp",EDGE,"E114.MirrorCS"),sQuery(id+"F0.wireOp",EDGE,"E133.MirrorCS"),sQuery(id+"F0.wireOp",EDGE,"E166.MirrorCS"),sQuery(id+"F0.wireOp",EDGE,"E116.MirrorCS"),sQuery(id+"F0.wireOp",EDGE,"E167.MirrorCS"),sQuery(id+"F0.wireOp",EDGE,"E120.MirrorCS"),sQuery(id+"F0.wireOp",EDGE,"E137.MirrorCS"),sQuery(id+"F0.wireOp",EDGE,"E119.MirrorCS"),sQuery(id+"F0.wireOp",EDGE,"E168.MirrorCS"),sQuery(id+"F0.wireOp",EDGE,"E142.MirrorCS"),sQuery(id+"F0.wireOp",EDGE,"E169.MirrorCS"),sQuery(id+"F0.wireOp",EDGE,"E151.MirrorCS"),sQuery(id+"F0.wireOp",EDGE,"E127.MirrorCS"),sQuery(id+"F0.wireOp",EDGE,"E136.MirrorCS"),sQuery(id+"F0.wireOp",EDGE,"E121.MirrorCS"),sQuery(id+"F0.wireOp",EDGE,"E126.MirrorCS"),sQuery(id+"F0.wireOp",EDGE,"E170.MirrorCS"),sQuery(id+"F0.wireOp",EDGE,"E90.MirrorCS"),sQuery(id+"F0.wireOp",EDGE,"E145.MirrorCS"),sQuery(id+"F0.wireOp",EDGE,"E128.MirrorCS"),sQuery(id+"F0.wireOp",EDGE,"E153.MirrorCS"),sQuery(id+"F0.wireOp",EDGE,"E152.MirrorCS"),sQuery(id+"F0.wireOp",EDGE,"E148.MirrorCS"),sQuery(id+"F0.wireOp",EDGE,"E155.MirrorCS"),sQuery(id+"F0.wireOp",EDGE,"E171.MirrorCS"),sQuery(id+"F0.wireOp",EDGE,"E172.MirrorCS"),sQuery(id+"F0.wireOp",EDGE,"E154.MirrorCS"),sQuery(id+"F0.wireOp",EDGE,"E173.MirrorCS"),sQuery(id+"F0.wireOp",EDGE,"E159.MirrorCS"),sQuery(id+"F0.wireOp",EDGE,"E123.MirrorCS"),sQuery(id+"F0.wireOp",EDGE,"E157.MirrorCS"),sQuery(id+"F0.wireOp",EDGE,"E132.MirrorCS"),sQuery(id+"F0.wireOp",EDGE,"E147.MirrorCS"),sQuery(id+"F0.wireOp",EDGE,"E174.MirrorCS"),sQuery(id+"F0.wireOp",EDGE,"E156.MirrorCS"),sQuery(id+"F0.wireOp",EDGE,"E141.MirrorCS"),sQuery(id+"F0.wireOp",EDGE,"E92.MirrorCS"),sQuery(id+"F0.wireOp",EDGE,"E131.MirrorCS"),sQuery(id+"F0.wireOp",EDGE,"E122.MirrorCS"),sQuery(id+"F0.wireOp",EDGE,"E135.MirrorCS"),sQuery(id+"F0.wireOp",EDGE,"E125.MirrorCS"),sQuery(id+"F0.wireOp",EDGE,"E91.MirrorCS"),sQuery(id+"F0.wireOp",EDGE,"E150.MirrorCS"),sQuery(id+"F0.wireOp",EDGE,"E124.MirrorCS"),sQuery(id+"F0.wireOp",EDGE,"E158.MirrorCS"),sQuery(id+"F0.wireOp",EDGE,"E134.MirrorCS"),sQuery(id+"F0.wireOp",EDGE,"E93.MirrorCS"),sQuery(id+"F0.wireOp",EDGE,"E139.MirrorCS"),sQuery(id+"F0.wireOp",EDGE,"E138.MirrorCS"),sQuery(id+"F0.wireOp",EDGE,"E143.MirrorCS"),sQuery(id+"F0.wireOp",EDGE,"E130.MirrorCS"),sQuery(id+"F0.wireOp",EDGE,"E129.MirrorCS"),sQuery(id+"F0.wireOp",EDGE,"E175"),sQuery(id+"F0.wireOp",EDGE,"E176")])],"isStart":false});
            chamfer(context, id + "F3", {"entities" : qUnion([Q0, Q1]), "width" : 2.3 * mm, "tangentPropagation" : true});
        }
    });
